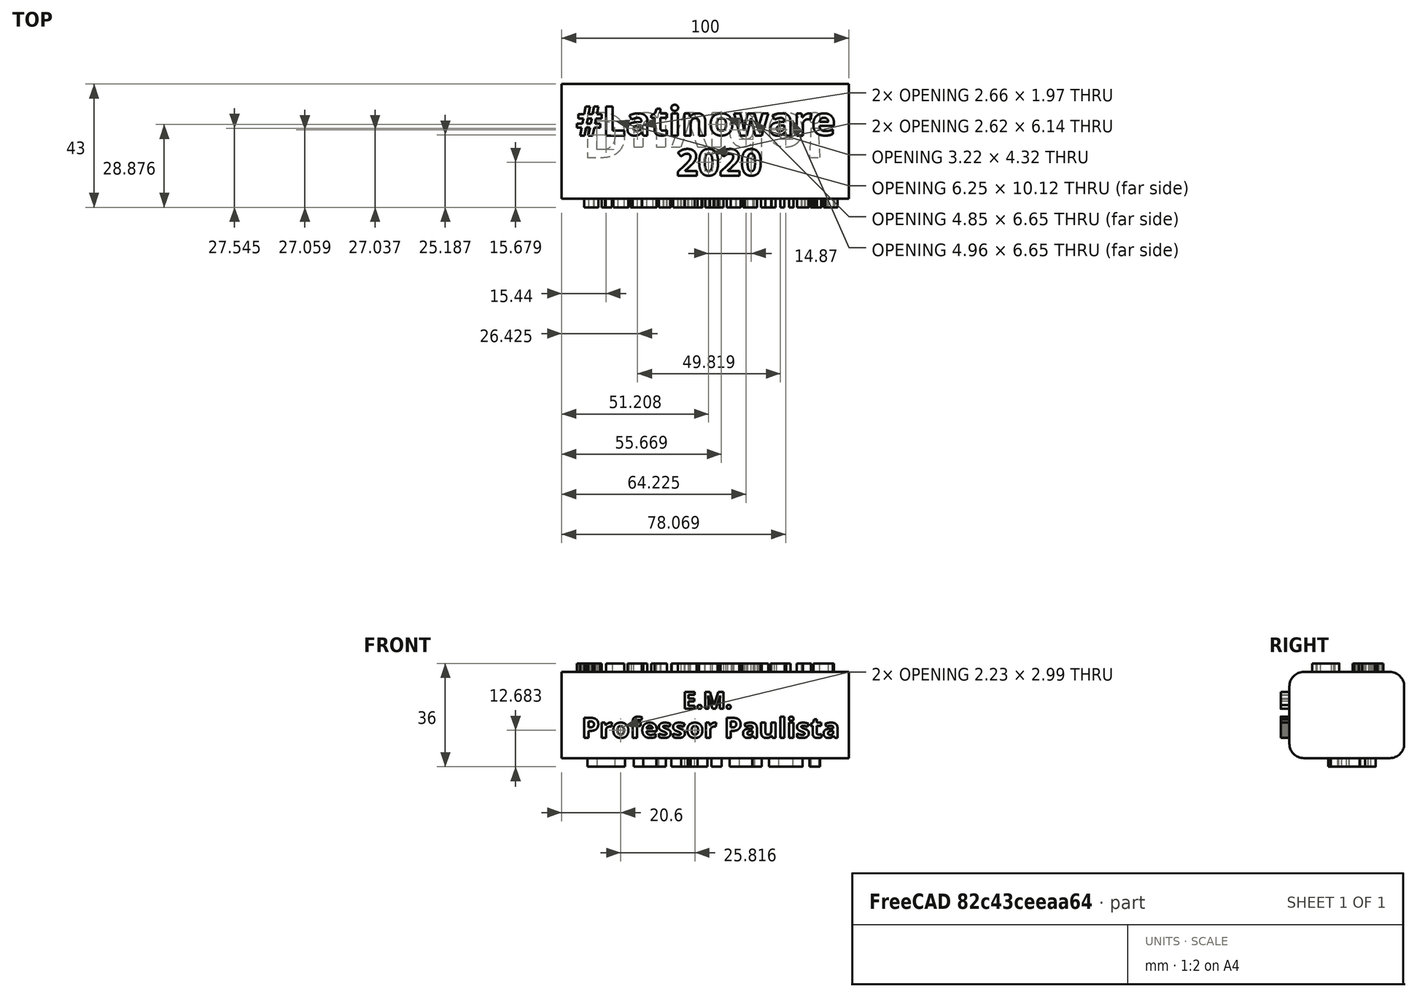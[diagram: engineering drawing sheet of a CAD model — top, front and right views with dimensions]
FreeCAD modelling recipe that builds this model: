
FCSTD DOCUMENT  (FreeCAD 0.19R)
Label: DUVIDO-0
License: Creative Commons Attribution-NonCommercial
LicenseURL: http://creativecommons.org/licenses/by-nc/4.0/
objects: Part::Extrusion×6, Part::Part2DObjectPython×5, Sketcher::SketchObject×1, Part::MultiFuse×1
note: 13 computed .brp shape members not serialized (recipe doc carries the construction recipe); baked Part::Feature solids carry a one-line shape summary decoded from their .brp

FEATURE [Part::Part2DObjectPython] ShapeString  # Draft 2D object (typed FeaturePython)
  FontFile = <path>
  Placement = pos=(1,0,0) rot=(0,0,1;0rad)
  Size = 7.5
  String = E.M.
  Tracking = 0
FEATURE [Part::Part2DObjectPython] ShapeString001  # Draft 2D object (typed FeaturePython)
  FontFile = <path>
  Placement = pos=(5,7,0) rot=(0,0,1;0rad)
  Size = 13
  String = #Latinoware
  Tracking = 0
FEATURE [Part::Extrusion] Extrude
  Base = -> ShapeString
  Dir = (0,0,1)
  DirMode = 2
  FaceMakerClass = Part::FaceMakerBullseye
  LengthFwd = 3
  LengthRev = 0
  Placement = pos=(41.2015,-15,-12.85) rot=(1,0,0;1.5708rad)
  Solid = false
  Symmetric = false
FEATURE [Part::Extrusion] Extrude001
  Base = -> ShapeString001
  Dir = (0,0,1)
  DirMode = 2
  FaceMakerClass = Part::FaceMakerBullseye
  LengthFwd = 3
  LengthRev = 0
  Solid = false
  Symmetric = false
FEATURE [Sketcher::SketchObject] Sketch
  Placement = pos=(0,0,0) rot=(0.57735,0.57735,0.57735;2.0944rad)
  sketch-geometry (12):
    g0: LineSegment StartX=-10 StartY=0 StartZ=0 EndX=20 EndY=0 EndZ=0
    g1: LineSegment StartX=25 StartY=-5 StartZ=0 EndX=25 EndY=-25 EndZ=0
    g2: LineSegment StartX=20 StartY=-30 StartZ=0 EndX=-10 EndY=-30 EndZ=0
    g3: LineSegment StartX=-15 StartY=-25 StartZ=0 EndX=-15 EndY=-5 EndZ=0
    g4: ArcOfCircle CenterX=20 CenterY=-5 CenterZ=0 NormalX=0 NormalY=0 NormalZ=1 AngleXU=0 Radius=5 StartAngle=0 EndAngle=1.5708
    g5: ArcOfCircle CenterX=20 CenterY=-25 CenterZ=0 NormalX=0 NormalY=0 NormalZ=1 AngleXU=0 Radius=5 StartAngle=4.71239 EndAngle=6.28319
    g6: ArcOfCircle CenterX=-10 CenterY=-25 CenterZ=0 NormalX=0 NormalY=0 NormalZ=1 AngleXU=0 Radius=5 StartAngle=3.14159 EndAngle=4.71239
    g7: ArcOfCircle CenterX=-10 CenterY=-5 CenterZ=0 NormalX=0 NormalY=0 NormalZ=1 AngleXU=0 Radius=5 StartAngle=1.5708 EndAngle=3.14159
    g8: LineSegment [constr] StartX=-10 StartY=-5 StartZ=0 EndX=20 EndY=-5 EndZ=0
    g9: LineSegment [constr] StartX=20 StartY=-5 StartZ=0 EndX=20 EndY=-25 EndZ=0
    g10: LineSegment [constr] StartX=20 StartY=-25 StartZ=0 EndX=-10 EndY=-25 EndZ=0
    g11: LineSegment [constr] StartX=-10 StartY=-25 StartZ=0 EndX=-10 EndY=-5 EndZ=0
  constraints (26):
    c: Horizontal(g0)
    c: Horizontal(g2)
    c: Vertical(g1)
    c: Vertical(g3)
    c: Tangent(g0,g4) = 1.5708
    c: Tangent(g1,g4) = 1.5708
    c: Tangent(g1,g5) = 1.5708
    c: Tangent(g2,g5) = 1.5708
    c: Tangent(g2,g6) = 1.5708
    c: Tangent(g3,g6) = 1.5708
    c: Tangent(g3,g7) = 1.5708
    c: Tangent(g0,g7) = 1.5708
    c: Coincident(g8,g9)
    c: Coincident(g9,g10)
    c: Coincident(g10,g11)
    c: Coincident(g11,g8)
    c: Horizontal(g8)
    c: Horizontal(g10)
    c: Vertical(g9)
    c: Coincident(g8,g7)
    c: Coincident(g9,g5)
    c: Coincident(g4,g8)
    c: Coincident(g6,g10)
    c: DistanceX(g10,g10) = 30
    c: DistanceY(g9,g9) = 20
    c: Radius(g4) = 5
FEATURE [Part::Extrusion] Extrude004
  Base = -> Sketch
  Dir = (1,0,0)
  DirMode = 2
  FaceMakerClass = Part::FaceMakerBullseye
  LengthFwd = 100
  LengthRev = 0
  Solid = true
  Symmetric = false
FEATURE [Part::Part2DObjectPython] ShapeString003  # Draft 2D object (typed FeaturePython)
  FontFile = <path>
  Placement = pos=(1,0,0) rot=(0,0,1;0rad)
  Size = 9
  String = Professor Paulista
  Tracking = 0
FEATURE [Part::Extrusion] Extrude005
  Base = -> ShapeString003
  Dir = (0,0,1)
  DirMode = 2
  FaceMakerClass = Part::FaceMakerBullseye
  LengthFwd = 3
  LengthRev = 0
  Placement = pos=(6,-15,-23) rot=(1,0,0;1.5708rad)
  Solid = false
  Symmetric = false
FEATURE [Part::MultiFuse] Fusion
  Refine = true
  Shapes = -> [Extrude,Extrude005]
FEATURE [Part::Part2DObjectPython] ShapeString004  # Draft 2D object (typed FeaturePython)
  FontFile = <path>
  Placement = pos=(7,15,-30) rot=(1,0,0;3.14159rad)
  Size = 20
  String = Duvido!
  Tracking = 0
FEATURE [Part::Extrusion] Extrude006
  Base = -> ShapeString004
  Dir = (0,-1e-16,-1)
  DirMode = 2
  FaceMakerClass = Part::FaceMakerBullseye
  LengthFwd = 3
  LengthRev = 0
  Solid = false
  Symmetric = false
FEATURE [Part::Part2DObjectPython] ShapeString005  # Draft 2D object (typed FeaturePython)
  FontFile = <path>
  Placement = pos=(40,-7,0) rot=(0,0,1;0rad)
  Size = 12
  String = 2020
  Tracking = 0
FEATURE [Part::Extrusion] Extrude007
  Base = -> ShapeString005
  Dir = (0,0,1)
  DirMode = 2
  FaceMakerClass = Part::FaceMakerBullseye
  LengthFwd = 3
  LengthRev = 0
  Solid = false
  Symmetric = false
note: 5 file-system paths scrubbed to <path> (originals preserved in the JSON sidecar)
